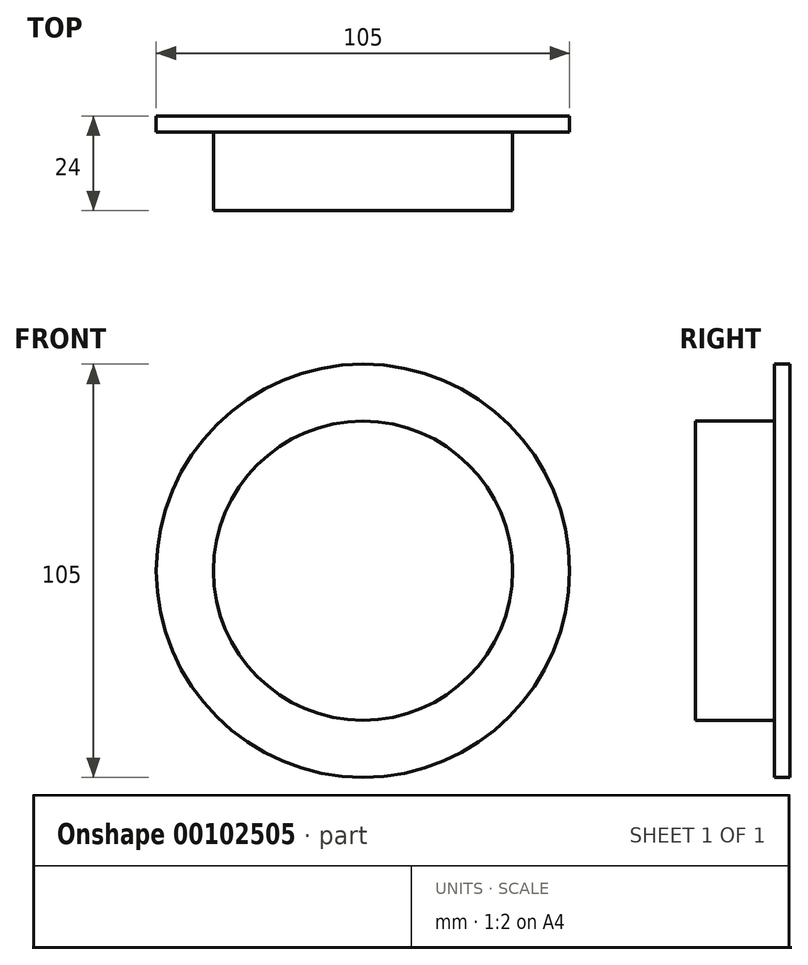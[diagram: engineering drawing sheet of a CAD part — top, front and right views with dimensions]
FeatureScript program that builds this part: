
annotation { "Feature Type Name" : "Feature", "Feature Type Description" : "" }
export const myFeature = defineFeature(function(context is Context, id is Id, definition is map)
    precondition{}
    {
        {
            var Q0;
            Q0=qCreatedBy(makeId("Right.planeOp"),FACE);
            var sketch = newSketch(context, id + "F0", { "sketchPlane" : qUnion([Q0])});
            skLineSegment(sketch, "E0", {"start": v(0, 0) * mm, "end": v(0, 38) * mm});
            skLineSegment(sketch, "E1", {"start": v(0, 38) * mm, "end": v(20, 38) * mm});
            skLineSegment(sketch, "E2", {"start": v(20, 38) * mm, "end": v(20, 52.5) * mm});
            skLineSegment(sketch, "E3", {"start": v(20, 52.5) * mm, "end": v(24, 52.5) * mm});
            skLineSegment(sketch, "E4", {"start": v(24, 52.5) * mm, "end": v(24, 0) * mm});
            skLineSegment(sketch, "E5", {"start": v(24, 0) * mm, "end": v(0, 0) * mm});
            skLineSegment(sketch, "E6", {"start": v(0, 0) * mm, "end": v(-33.25, 0) * mm, "construction": true});
            skSolve(sketch);
        }
        {
            var Q0;
            Q0=makeQuery(id+"F0.imprint","IMPRINT",FACE,{"disambiguationData":[TD([[makeQuery(id+"F0.imprint","IMPRINT",EDGE,{"derivedFrom":sQuery(id+"F0.wireOp",EDGE,"E0")}),-1.0]])]});
            var Q1;
            Q1=sQuery(id+"F0.wireOp",EDGE,"E6");
            revolve(context, id + "F1", {"entities" : qUnion([Q0]), "axis" : qUnion([Q1]), "revolveType" : RevolveType.FULL});
        }
    });
